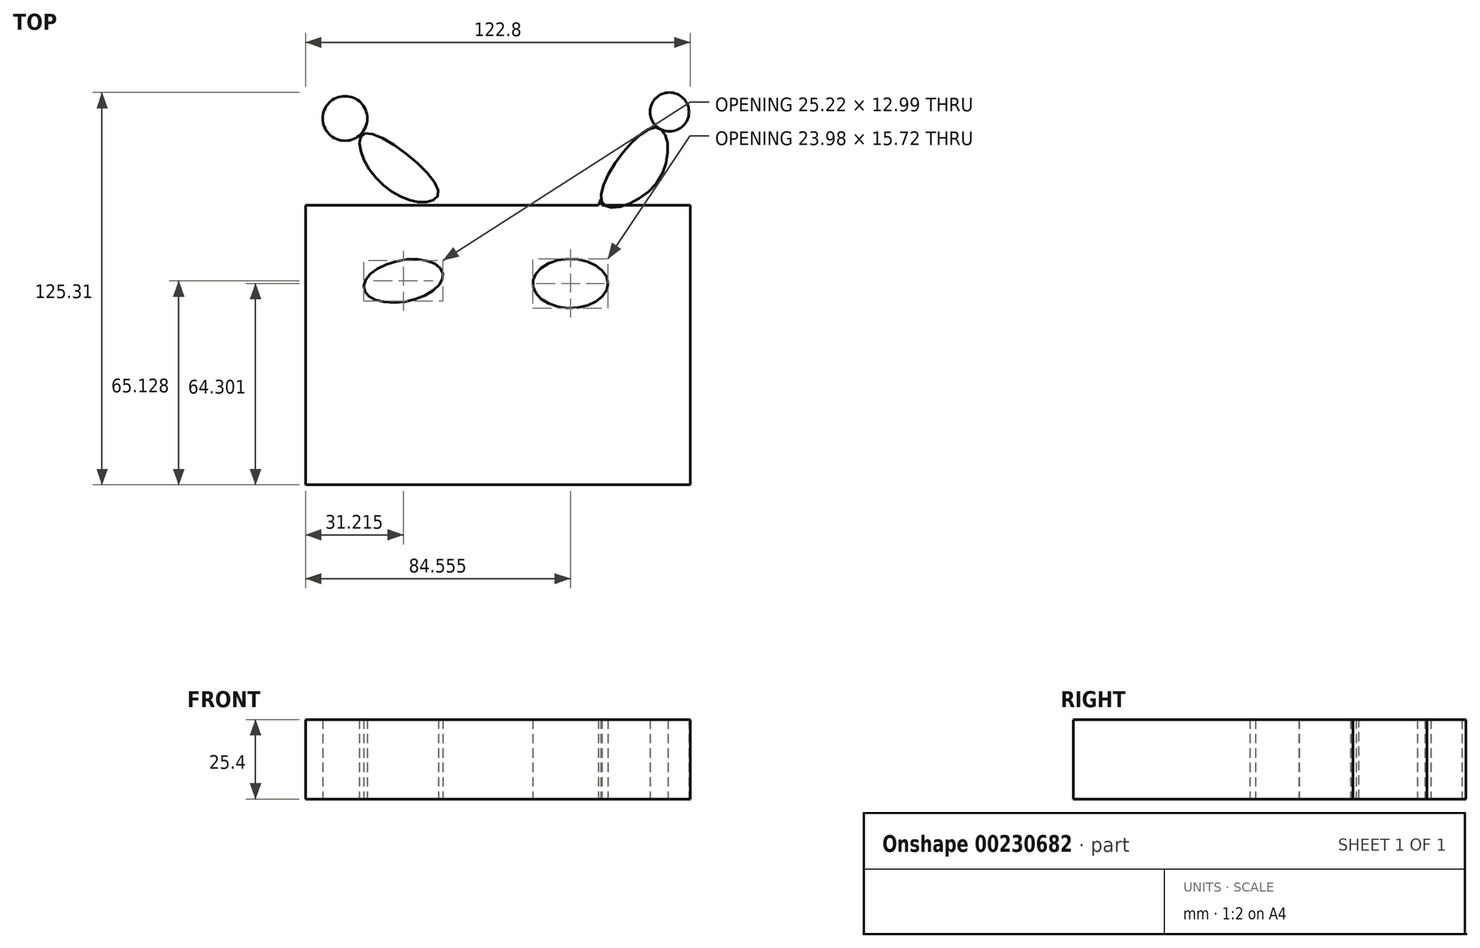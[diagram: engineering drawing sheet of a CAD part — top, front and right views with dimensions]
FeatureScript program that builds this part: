
annotation { "Feature Type Name" : "Feature", "Feature Type Description" : "" }
export const myFeature = defineFeature(function(context is Context, id is Id, definition is map)
    precondition{}
    {
        {
            var Q0;
            Q0=qCreatedBy(makeId("Top.planeOp"),FACE);
            var sketch = newSketch(context, id + "F0", { "sketchPlane" : qUnion([Q0])});
            skLineSegment(sketch, "E0.bottom", {"start": v(61.4, -44.66) * mm, "end": v(-61.4, -44.66) * mm});
            skLineSegment(sketch, "E0.top", {"start": v(61.4, 44.66) * mm, "end": v(-61.4, 44.66) * mm});
            skLineSegment(sketch, "E0.left", {"start": v(61.4, -44.66) * mm, "end": v(61.4, 44.66) * mm});
            skLineSegment(sketch, "E0.right", {"start": v(-61.4, -44.66) * mm, "end": v(-61.4, 44.66) * mm});
            skPoint(sketch, "E0.middle", {"position": v(0, 0) * mm});
            skEllipse(sketch, "E1", {"center": v(23.16, 19.64) * mm, "majorRadius": 12 * mm, "minorRadius": 7.86 * mm, "majorAxis": v(1, 0)});
            skEllipse(sketch, "E2", {"center": v(-30.18, 20.47) * mm, "majorRadius": 12.85 * mm, "minorRadius": 6.62 * mm, "majorAxis": v(0.98, 0.2)});
            skFitSpline(sketch, "E3", {"points": [v(24.18, 46.52) * mm, v(48.59, 70.3) * mm, v(54.58, 67.6) * mm, v(54.8, 67.6) * mm], "startDerivative": vector(40.45, 54.38) * mm, "endDerivative": vector(2.88, 1.3) * mm});
            skFitSpline(sketch, "E4", {"points": [v(54.8, 67.6) * mm, v(31.63, 44.66) * mm, v(32.04, 44.66) * mm, v(32.87, 46.52) * mm, v(33.28, 44.66) * mm], "startDerivative": vector(-56.67, -52.1) * mm, "endDerivative": vector(2.31, -19.84) * mm});
            skFitSpline(sketch, "E5", {"points": [v(-19.04, 49.41) * mm, v(-42.2, 67.6) * mm, v(-41.79, 57.27) * mm, v(-25.04, 45.65) * mm, v(-19.04, 49.41) * mm]});
            skCircle(sketch, "E6", {"center": v(-48.82, 72.36) * mm, "radius": 7.13 * mm});
            skCircle(sketch, "E7", {"center": v(54.8, 74.43) * mm, "radius": 6.22 * mm});
            skSolve(sketch);
        }
        {
            var Q0;
            Q0 = qSketchRegion(id + "F0", true);
            extrude(context, id + "F1", {"entities" : qUnion([Q0]), "depth" : 25.4 * mm});
        }
        {
            var Q0;
            Q0=qCreatedBy(makeId("Top.planeOp"),FACE);
            var sketch = newSketch(context, id + "F2", { "sketchPlane" : qUnion([Q0])});
            skFitSpline(sketch, "E8", {"points": [v(33.08, 45.9) * mm, v(50.24, 69.47) * mm, v(51.07, 52.3) * mm, v(33.08, 45.9) * mm]});
            skSolve(sketch);
        }
        {
            var Q0;
            Q0 = qSketchRegion(id + "F2", true);
            extrude(context, id + "F3", {"entities" : qUnion([Q0]), "depth" : 25.4 * mm});
        }
    });
